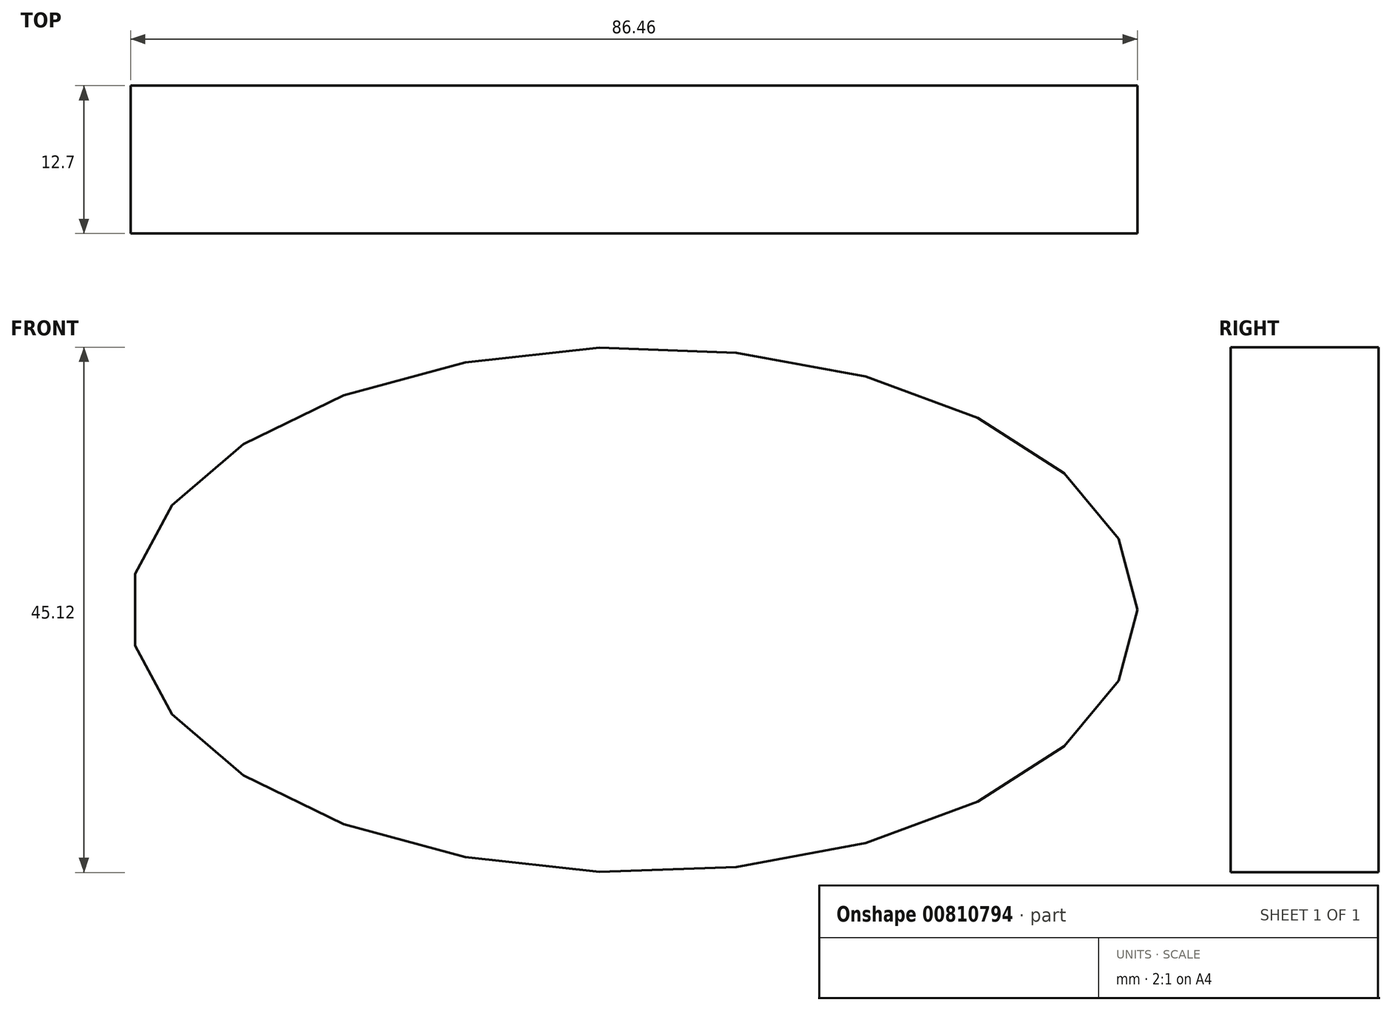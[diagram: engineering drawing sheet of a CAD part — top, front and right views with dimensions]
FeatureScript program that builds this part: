
annotation { "Feature Type Name" : "Feature", "Feature Type Description" : "" }
export const myFeature = defineFeature(function(context is Context, id is Id, definition is map)
    precondition{}
    {
        {
            var Q0;
            Q0=qCreatedBy(makeId("Front.planeOp"),FACE);
            var sketch = newSketch(context, id + "F0", { "sketchPlane" : qUnion([Q0])});
            skEllipse(sketch, "E0", {"center": v(0, 0) * mm, "majorRadius": 43.23 * mm, "minorRadius": 22.56 * mm, "majorAxis": v(1, 0)});
            skPoint(sketch, "E1.endSnap0", {"position": v(0, -22.56) * mm});
            skPoint(sketch, "E2.endSnap0", {"position": v(0, 22.56) * mm});
            skSolve(sketch);
        }
        {
            var Q0;
            Q0 = qSketchRegion(id + "F0", true);
            extrude(context, id + "F1", {"entities" : qUnion([Q0]), "depth" : 12.7 * mm, "offsetDistance" : 25.4 * mm});
        }
    });
